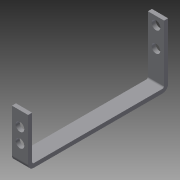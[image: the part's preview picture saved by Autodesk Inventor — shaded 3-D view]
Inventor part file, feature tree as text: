
AUTODESK INVENTOR PART (.ipt)
format: ipt  version: 2013 (Build 170138000, 138)  size: 207,872 bytes
history: native  units: in
note: dims shown in document units (in); Inventor stores cm internally (conversion verified against a paired STEP export)
features: other x8, sheet_metal_op x7, sketch x6, reference x2
ambient origin geometry x8: Origin, YZ Plane, XZ Plane, XY Plane, X Axis, Y Axis, Z Axis, Center Point
bodies: Solid1 (feature_tree)
feature tree (23):
  sheet_metal_op  "Face1"
  sheet_metal_op  "Flange1"
  sheet_metal_op  "Flange2"
  sketch  "Sketch1"  dims[d0=0.5in]
  other  "Plate1"
  sketch  "Sketch2"  dims[d1=1.75in]
  other  "Plate2"
  sheet_metal_op  "Bend1"
  sheet_metal_op  "Corner1"
  sketch  "Sketch3"  dims[d2=0.125in]
  reference  "Reference1"
  reference  "Reference2"
  sketch  "Sketch5"  dims[d4=0.0625in]
  other  "Plate3"
  sheet_metal_op  "Bend2"
  sheet_metal_op  "Corner2"
  sketch  "Sketch6"  dims[d5=0.25in d6=0.125in d7=4.1472in d8=90.0deg d9=0.05in d10=0.5in d11=0.125in d12=0.125in d13=0.125in d14=0.0in d19=0.125in d20=0.0625in d21=0.25in d22=0.125in d23=1.5in d24=90.0deg d25=0.05in d26=0.5in d27=0.125in d28=0.125in d29=0.4417in d31=0.442in d32=0.266in d33=0.266in d34=0.125in d35=0.0in d15=0.0625in d16=0.125in d17=0.0in d18=0.125in]
  other  "Cut1"
  other  "Cut3"
  other  "Definition1"
  sketch  "Sketch4"  dims[d3=0.125in]
  other  "Cut2"
  other  "Cut4"
